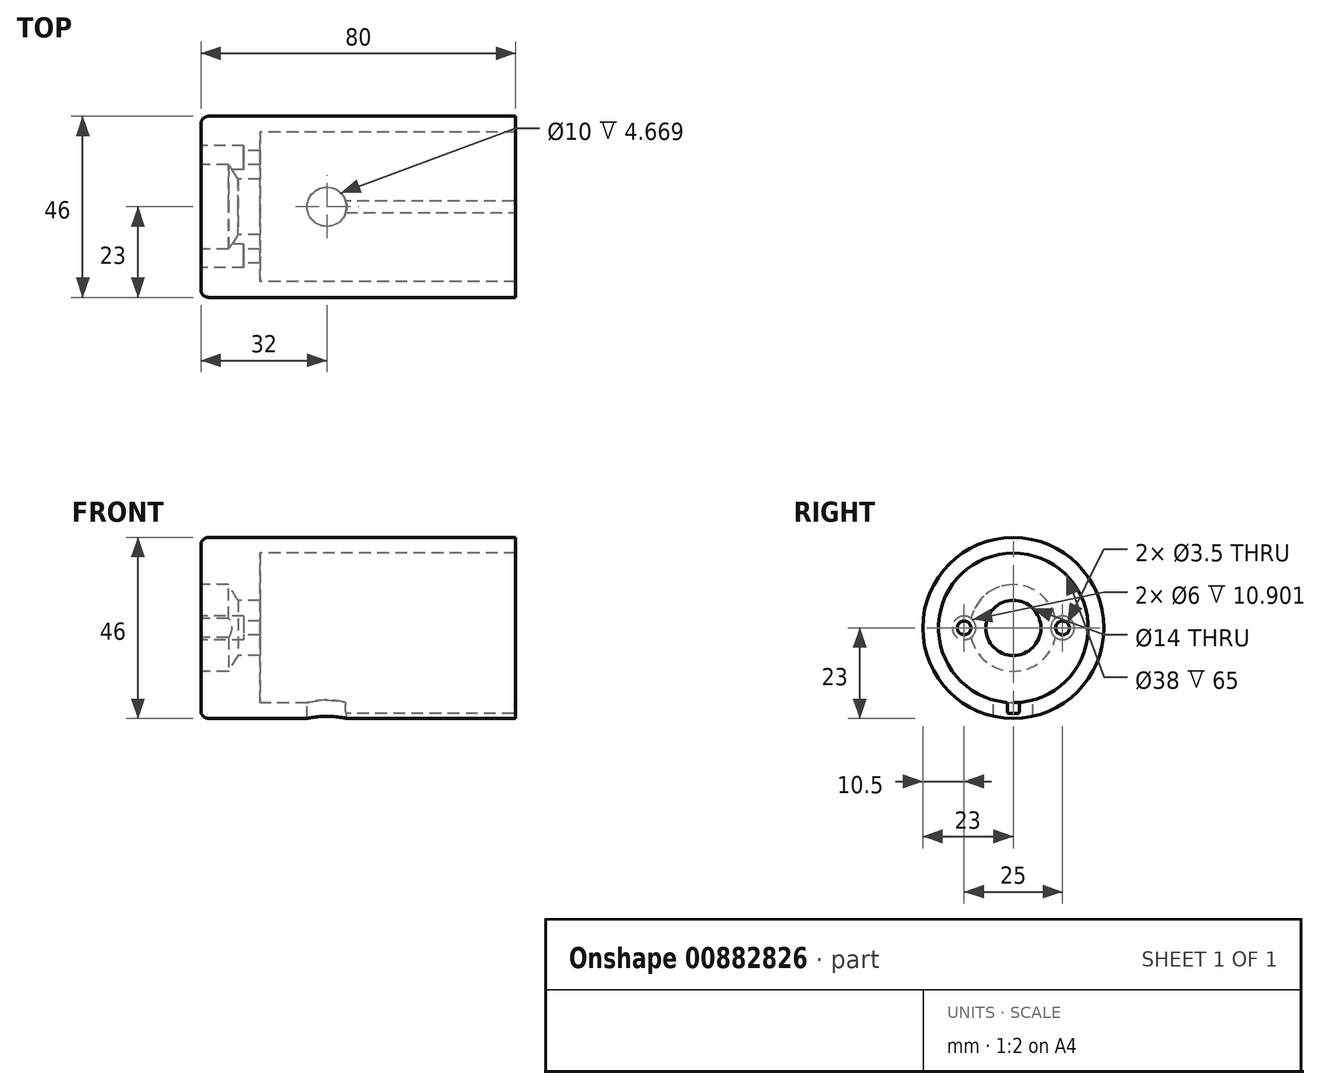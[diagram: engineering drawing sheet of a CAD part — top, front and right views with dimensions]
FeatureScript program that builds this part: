
annotation { "Feature Type Name" : "Feature", "Feature Type Description" : "" }
export const myFeature = defineFeature(function(context is Context, id is Id, definition is map)
    precondition{}
    {
        {
            var Q0;
            Q0=qCreatedBy(makeId("Right.planeOp"),FACE);
            var sketch = newSketch(context, id + "F0", { "sketchPlane" : qUnion([Q0])});
            skCircle(sketch, "E0", {"center": v(0, 0) * mm, "radius": 23 * mm});
            skCircle(sketch, "E1", {"center": v(0, 0) * mm, "radius": 19 * mm});
            skPoint(sketch, "E2", {"position": v(0, -23) * mm});
            skLineSegment(sketch, "E3", {"start": v(0, -23) * mm, "end": v(0, -18.78) * mm});
            skLineSegment(sketch, "E4", {"start": v(0, -18.78) * mm, "end": v(1.5, -18.78) * mm});
            skLineSegment(sketch, "E5", {"start": v(1.5, -18.78) * mm, "end": v(1.5, -21.78) * mm});
            skLineSegment(sketch, "E6", {"start": v(1.5, -21.78) * mm, "end": v(-1.5, -21.78) * mm});
            skLineSegment(sketch, "E7", {"start": v(-1.5, -21.78) * mm, "end": v(-1.5, -18.78) * mm});
            skLineSegment(sketch, "E8", {"start": v(-1.5, -18.78) * mm, "end": v(0, -18.78) * mm});
            skLineSegment(sketch, "E9", {"start": v(0, 0) * mm, "end": v(12.5, 0) * mm});
            skLineSegment(sketch, "E10", {"start": v(0, 0) * mm, "end": v(-12.5, 0) * mm});
            skSolve(sketch);
        }
        {
            var Q0;
            Q0=makeQuery(id+"F0.imprint","IMPRINT",FACE,{"disambiguationData":[TD([[makeQuery(id+"F0.imprint","IMPRINT",EDGE,{"derivedFrom":sQuery(id+"F0.wireOp",EDGE,"E0")}),1.0]])]});
            extrude(context, id + "F1", {"entities" : qUnion([Q0]), "depth" : 80 * mm, "offsetDistance" : 25 * mm});
        }
        {
            var Q0;
            Q0=qSketchRegion(id+"F0",true);
            var Q1;
            {var subQ1=sQuery(id+"F0.wireOp",EDGE,"E4");Q1=makeQuery(id+"F0.imprint","IMPRINT",FACE,{"disambiguationData":[TD([[makeQuery(id+"F0.imprint","IMPRINT",EDGE,{"derivedFrom":subQ1}),1.0]])]});}
            var Q2;
            {var subQ0=sQuery(id+"F0.wireOp",EDGE,"E3");Q2=makeQuery(id+"F0.imprint","IMPRINT",FACE,{"disambiguationData":[TD([[makeQuery(id+"F0.imprint","IMPRINT",EDGE,{"derivedFrom":subQ0}),1.0]])]});}
            var Q3;
            {var subQ0=sQuery(id+"F0.wireOp",EDGE,"E3");Q3=makeQuery(id+"F0.imprint","IMPRINT",FACE,{"disambiguationData":[TD([[makeQuery(id+"F0.imprint","IMPRINT",EDGE,{"derivedFrom":subQ0}),-1.0]])]});}
            extrude(context, id + "F2", {"entities" : qUnion([Q0, Q1, Q2, Q3]), "operationType" : NewBodyOperationType.ADD, "depth" : 15 * mm, "offsetDistance" : 25 * mm});
        }
        {
            var Q0;
            Q0=qCreatedBy(makeId("Top.planeOp"),FACE);
            var sketch = newSketch(context, id + "F3", { "sketchPlane" : qUnion([Q0])});
            skLineSegment(sketch, "E11", {"start": v(0, 0) * mm, "end": v(32, 0) * mm});
            skSolve(sketch);
        }
        {
            var Q0;
            {var subQ0=sQuery(id+"F0.wireOp",EDGE,"E6");Q0=makeQuery(id+"F0.imprint","IMPRINT",FACE,{"disambiguationData":[TD([[makeQuery(id+"F0.imprint","IMPRINT",EDGE,{"derivedFrom":subQ0}),-1.0]])]});}
            extrude(context, id + "F4", {"entities" : qUnion([Q0]), "operationType" : NewBodyOperationType.ADD, "depth" : 28 * mm, "offsetDistance" : 25 * mm});
        }
        {
            var Q0;
            Q0=sQuery(id+"F3.wireOp",VERTEX,"E11.end");
            var Q1;
            Q1=makeQuery(id+"F1.opExtrude","SWEPT_BODY",BODY,{"disambiguationData":[OSD([sQuery(id+"F0.wireOp",EDGE,"E0"),sQuery(id+"F0.wireOp",EDGE,"E1"),sQuery(id+"F0.wireOp",EDGE,"E5"),sQuery(id+"F0.wireOp",EDGE,"E6"),sQuery(id+"F0.wireOp",EDGE,"E7")])]});
            hole(context, id + "F5", {"style" : HoleStyle.SIMPLE, "endStyle" : HoleEndStyle.THROUGH, "holeDiameter" : 10 * mm, "majorDiameter" : 5 * mm, "isTappedThrough" : true, "tappedDepth" : 12 * mm, "tapClearance" : 3, "locations" : qUnion([Q0]), "scope" : qUnion([Q1])});
        }
        {
            var Q0;
            Q0=sQuery(id+"F0.wireOp",VERTEX,"E0.center");
            var Q1;
            Q1=makeQuery(id+"F1.opExtrude","SWEPT_BODY",BODY,{"disambiguationData":[OSD([sQuery(id+"F0.wireOp",EDGE,"E0"),sQuery(id+"F0.wireOp",EDGE,"E1"),sQuery(id+"F0.wireOp",EDGE,"E5"),sQuery(id+"F0.wireOp",EDGE,"E6"),sQuery(id+"F0.wireOp",EDGE,"E7")])]});
            hole(context, id + "F6", {"style" : HoleStyle.SIMPLE, "endStyle" : HoleEndStyle.THROUGH, "oppositeDirection" : true, "holeDiameter" : 14 * mm, "majorDiameter" : 5 * mm, "isTappedThrough" : true, "tappedDepth" : 12 * mm, "tapClearance" : 3, "locations" : qUnion([Q0]), "scope" : qUnion([Q1])});
        }
        {
            var Q0;
            Q0=sQuery(id+"F0.wireOp",VERTEX,"E0.center");
            var Q1;
            Q1=makeQuery(id+"F1.opExtrude","SWEPT_BODY",BODY,{"disambiguationData":[OSD([sQuery(id+"F0.wireOp",EDGE,"E0"),sQuery(id+"F0.wireOp",EDGE,"E1"),sQuery(id+"F0.wireOp",EDGE,"E5"),sQuery(id+"F0.wireOp",EDGE,"E6"),sQuery(id+"F0.wireOp",EDGE,"E7")])]});
            hole(context, id + "F7", {"style" : HoleStyle.SIMPLE, "endStyle" : HoleEndStyle.BLIND, "oppositeDirection" : true, "holeDiameter" : 22 * mm, "majorDiameter" : 5 * mm, "holeDepth" : 7 * mm, "isTappedThrough" : true, "tappedDepth" : 12 * mm, "tapClearance" : 3, "locations" : qUnion([Q0]), "scope" : qUnion([Q1])});
        }
        {
            var Q0;
            Q0=sQuery(id+"F0.wireOp",VERTEX,"E9.end");
            var Q1;
            Q1=sQuery(id+"F0.wireOp",VERTEX,"E10.end");
            var Q2;
            Q2=makeQuery(id+"F1.opExtrude","SWEPT_BODY",BODY,{"disambiguationData":[OSD([sQuery(id+"F0.wireOp",EDGE,"E0"),sQuery(id+"F0.wireOp",EDGE,"E1"),sQuery(id+"F0.wireOp",EDGE,"E5"),sQuery(id+"F0.wireOp",EDGE,"E6"),sQuery(id+"F0.wireOp",EDGE,"E7")])]});
            hole(context, id + "F8", {"style" : HoleStyle.C_BORE, "endStyle" : HoleEndStyle.THROUGH, "oppositeDirection" : true, "holeDiameter" : 3.5 * mm, "cBoreDiameter" : 6 * mm, "cBoreDepth" : 3 * mm, "majorDiameter" : 5 * mm, "isTappedThrough" : true, "tappedDepth" : 12 * mm, "tapClearance" : 3, "locations" : qUnion([Q0, Q1]), "scope" : qUnion([Q2])});
        }
        {
            var Q0;
            Q0=makeQuery(id+"F2.boolean.opBoolean","SPLIT",EDGE,{"derivedFrom":makeQuery(id+"F1.opExtrude","SWEPT_EDGE",EDGE,{"disambiguationData":[OSD([sQuery(id+"F0.wireOp",EDGE,"E0"),sQuery(id+"F0.wireOp",EDGE,"E5")])]})});
            var Q1;
            Q1=makeQuery(id+"F2.boolean.opBoolean","SPLIT",EDGE,{"derivedFrom":makeQuery(id+"F1.opExtrude","SWEPT_EDGE",EDGE,{"disambiguationData":[OSD([sQuery(id+"F0.wireOp",EDGE,"E0"),sQuery(id+"F0.wireOp",EDGE,"E7")])]})});
            var Q2;
            Q2=makeQuery(id+"F1.opExtrude","CAP_EDGE",EDGE,{"disambiguationData":[OSD([sQuery(id+"F0.wireOp",EDGE,"E5")])],"isStart":false});
            var Q3;
            Q3=makeQuery(id+"F1.opExtrude","CAP_EDGE",EDGE,{"disambiguationData":[OSD([sQuery(id+"F0.wireOp",EDGE,"E7")])],"isStart":false});
            var Q4;
            Q4=makeQuery(id+"F7.hole-0.boolean.opBoolean","COPY",EDGE,{"derivedFrom":makeQuery(id+"F7.hole-0.opRevolve","SWEPT_EDGE",EDGE,{"disambiguationData":[OSD([sQuery(id+"F7.hole-0.sketch.wireOp",EDGE,"core_line_2"),sQuery(id+"F7.hole-0.sketch.wireOp",EDGE,"core_line_3")])]})});
            var Q5;
            Q5=makeQuery(id+"F7.hole-0.boolean.opBoolean","INTERSECT",EDGE,{"derivedFrom":[makeQuery(id+"F6.hole-0.boolean.opBoolean","COPY",FACE,{"derivedFrom":makeQuery(id+"F6.hole-0.opRevolve","SWEPT_FACE",FACE,{"disambiguationData":[OSD([sQuery(id+"F6.hole-0.sketch.wireOp",EDGE,"core_line_2")])]})}),makeQuery(id+"F7.hole-0.opRevolve","SWEPT_FACE",FACE,{"disambiguationData":[OSD([sQuery(id+"F7.hole-0.sketch.wireOp",EDGE,"core_line_1")])]})]});
            var Q6;
            Q6=makeQuery(id+"F6.hole-0.boolean.opBoolean","INTERSECT",EDGE,{"derivedFrom":[makeQuery(id+"F2.opExtrude","CAP_FACE",FACE,{"disambiguationData":[OSD([sQuery(id+"F0.wireOp",EDGE,"E0"),sQuery(id+"F0.wireOp",EDGE,"E1"),sQuery(id+"F0.wireOp",EDGE,"E5"),sQuery(id+"F0.wireOp",EDGE,"E6"),sQuery(id+"F0.wireOp",EDGE,"E7")])],"isStart":false}),makeQuery(id+"F6.hole-0.opRevolve","SWEPT_FACE",FACE,{"disambiguationData":[OSD([sQuery(id+"F6.hole-0.sketch.wireOp",EDGE,"core_line_2")])]})]});
            var Q7;
            Q7=makeQuery(id+"F8.hole-0.boolean.opBoolean","COPY",EDGE,{"derivedFrom":makeQuery(id+"F8.hole-0.opRevolve","SWEPT_EDGE",EDGE,{"disambiguationData":[OSD([sQuery(id+"F8.hole-0.sketch.wireOp",EDGE,"cbore_start_line_2"),sQuery(id+"F8.hole-0.sketch.wireOp",EDGE,"cbore_start_line_3")])]})});
            var Q8;
            Q8=makeQuery(id+"F8.hole-1.boolean.opBoolean","COPY",EDGE,{"derivedFrom":makeQuery(id+"F8.hole-1.opRevolve","SWEPT_EDGE",EDGE,{"disambiguationData":[OSD([sQuery(id+"F8.hole-1.sketch.wireOp",EDGE,"cbore_start_line_2"),sQuery(id+"F8.hole-1.sketch.wireOp",EDGE,"cbore_start_line_3")])]})});
            var Q9;
            Q9=makeQuery(id+"F8.hole-0.boolean.opBoolean","INTERSECT",EDGE,{"disambiguationData":[OD(1.0)],"derivedFrom":[makeQuery(id+"F7.hole-0.boolean.opBoolean","COPY",FACE,{"derivedFrom":makeQuery(id+"F7.hole-0.opRevolve","SWEPT_FACE",FACE,{"disambiguationData":[OSD([sQuery(id+"F7.hole-0.sketch.wireOp",EDGE,"core_line_2")])]})}),makeQuery(id+"F8.hole-0.opRevolve","SWEPT_FACE",FACE,{"disambiguationData":[OSD([sQuery(id+"F8.hole-0.sketch.wireOp",EDGE,"cbore_start_line_2")])]})]});
            var Q10;
            Q10=makeQuery(id+"F8.hole-0.boolean.opBoolean","INTERSECT",EDGE,{"disambiguationData":[OD(0.0)],"derivedFrom":[makeQuery(id+"F7.hole-0.boolean.opBoolean","COPY",FACE,{"derivedFrom":makeQuery(id+"F7.hole-0.opRevolve","SWEPT_FACE",FACE,{"disambiguationData":[OSD([sQuery(id+"F7.hole-0.sketch.wireOp",EDGE,"core_line_2")])]})}),makeQuery(id+"F8.hole-0.opRevolve","SWEPT_FACE",FACE,{"disambiguationData":[OSD([sQuery(id+"F8.hole-0.sketch.wireOp",EDGE,"cbore_start_line_2")])]})]});
            var Q11;
            Q11=makeQuery(id+"F8.hole-1.boolean.opBoolean","INTERSECT",EDGE,{"disambiguationData":[OD(1.0)],"derivedFrom":[makeQuery(id+"F7.hole-0.boolean.opBoolean","COPY",FACE,{"derivedFrom":makeQuery(id+"F7.hole-0.opRevolve","SWEPT_FACE",FACE,{"disambiguationData":[OSD([sQuery(id+"F7.hole-0.sketch.wireOp",EDGE,"core_line_2")])]})}),makeQuery(id+"F8.hole-1.opRevolve","SWEPT_FACE",FACE,{"disambiguationData":[OSD([sQuery(id+"F8.hole-1.sketch.wireOp",EDGE,"cbore_start_line_2")])]})]});
            var Q12;
            Q12=makeQuery(id+"F8.hole-1.boolean.opBoolean","INTERSECT",EDGE,{"disambiguationData":[OD(0.0)],"derivedFrom":[makeQuery(id+"F7.hole-0.boolean.opBoolean","COPY",FACE,{"derivedFrom":makeQuery(id+"F7.hole-0.opRevolve","SWEPT_FACE",FACE,{"disambiguationData":[OSD([sQuery(id+"F7.hole-0.sketch.wireOp",EDGE,"core_line_2")])]})}),makeQuery(id+"F8.hole-1.opRevolve","SWEPT_FACE",FACE,{"disambiguationData":[OSD([sQuery(id+"F8.hole-1.sketch.wireOp",EDGE,"cbore_start_line_2")])]})]});
            var Q13;
            Q13=makeQuery(id+"F8.hole-0.boolean.opBoolean","INTERSECT",EDGE,{"derivedFrom":[makeQuery(id+"F7.hole-0.boolean.opBoolean","COPY",FACE,{"derivedFrom":makeQuery(id+"F7.hole-0.opRevolve","SWEPT_FACE",FACE,{"disambiguationData":[OSD([sQuery(id+"F7.hole-0.sketch.wireOp",EDGE,"core_line_1")])]})}),makeQuery(id+"F8.hole-0.opRevolve","SWEPT_FACE",FACE,{"disambiguationData":[OSD([sQuery(id+"F8.hole-0.sketch.wireOp",EDGE,"cbore_start_line_2")])]})]});
            var Q14;
            Q14=makeQuery(id+"F8.hole-1.boolean.opBoolean","INTERSECT",EDGE,{"derivedFrom":[makeQuery(id+"F7.hole-0.boolean.opBoolean","COPY",FACE,{"derivedFrom":makeQuery(id+"F7.hole-0.opRevolve","SWEPT_FACE",FACE,{"disambiguationData":[OSD([sQuery(id+"F7.hole-0.sketch.wireOp",EDGE,"core_line_1")])]})}),makeQuery(id+"F8.hole-1.opRevolve","SWEPT_FACE",FACE,{"disambiguationData":[OSD([sQuery(id+"F8.hole-1.sketch.wireOp",EDGE,"cbore_start_line_2")])]})]});
            var Q15;
            Q15=makeQuery(id+"F8.hole-1.boolean.opBoolean","COPY",EDGE,{"derivedFrom":makeQuery(id+"F8.hole-1.opRevolve","SWEPT_EDGE",EDGE,{"disambiguationData":[OSD([sQuery(id+"F8.hole-1.sketch.wireOp",EDGE,"cbore_start_line_1"),sQuery(id+"F8.hole-1.sketch.wireOp",EDGE,"core_line_2")])]})});
            var Q16;
            Q16=makeQuery(id+"F8.hole-0.boolean.opBoolean","COPY",EDGE,{"derivedFrom":makeQuery(id+"F8.hole-0.opRevolve","SWEPT_EDGE",EDGE,{"disambiguationData":[OSD([sQuery(id+"F8.hole-0.sketch.wireOp",EDGE,"cbore_start_line_1"),sQuery(id+"F8.hole-0.sketch.wireOp",EDGE,"core_line_2")])]})});
            var Q17;
            Q17=makeQuery(id+"F8.hole-1.boolean.opBoolean","INTERSECT",EDGE,{"derivedFrom":[makeQuery(id+"F2.opExtrude","CAP_FACE",FACE,{"disambiguationData":[OSD([sQuery(id+"F0.wireOp",EDGE,"E0")])],"isStart":false}),makeQuery(id+"F8.hole-1.opRevolve","SWEPT_FACE",FACE,{"disambiguationData":[OSD([sQuery(id+"F8.hole-1.sketch.wireOp",EDGE,"core_line_2")])]})]});
            var Q18;
            Q18=makeQuery(id+"F8.hole-0.boolean.opBoolean","INTERSECT",EDGE,{"derivedFrom":[makeQuery(id+"F2.opExtrude","CAP_FACE",FACE,{"disambiguationData":[OSD([sQuery(id+"F0.wireOp",EDGE,"E0")])],"isStart":false}),makeQuery(id+"F8.hole-0.opRevolve","SWEPT_FACE",FACE,{"disambiguationData":[OSD([sQuery(id+"F8.hole-0.sketch.wireOp",EDGE,"core_line_2")])]})]});
            fillet(context, id + "F9", {"entities" : qUnion([Q0, Q1, Q2, Q3, Q4, Q5, Q6, Q7, Q8, Q9, Q10, Q11, Q12, Q13, Q14, Q15, Q16, Q17, Q18]), "radius" : 0.5 * mm, "tangentPropagation" : true, "allowEdgeOverflow" : false});
        }
        {
            var Q0;
            Q0=makeQuery(id+"F1.opExtrude","CAP_EDGE",EDGE,{"disambiguationData":[OSD([sQuery(id+"F0.wireOp",EDGE,"E1")])],"isStart":true});
            var Q1;
            Q1=makeQuery(id+"F1.opExtrude","CAP_EDGE",EDGE,{"disambiguationData":[OSD([sQuery(id+"F0.wireOp",EDGE,"E0")])],"isStart":true});
            fillet(context, id + "F10", {"entities" : qUnion([Q0, Q1]), "radius" : 2 * mm, "tangentPropagation" : true, "allowEdgeOverflow" : false});
        }
    });
